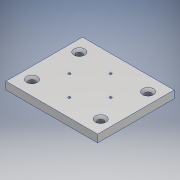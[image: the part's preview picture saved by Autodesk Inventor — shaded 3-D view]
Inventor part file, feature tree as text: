
AUTODESK INVENTOR PART (.ipt)
format: ipt  version: 2017 (Build 210142000, 142)  size: 131,072 bytes
history: native  units: mm
features: chamfer x3, sketch x3, hole x2, extrude x1
ambient origin geometry x8: Origin, YZ Plane, XZ Plane, XY Plane, X Axis, Y Axis, Z Axis, Center Point
bodies: Solid1 (feature_tree)
feature tree (9):
  extrude  "Extrusion1"  Depth=100.0mm
  hole  "Hole1"  [1 undecoded]
  chamfer  "Chamfer1"  Distance=3.0mm Angle=45.0deg
  chamfer  "Chamfer2"  Distance=3.0mm Angle=45.0deg
  hole  "Hole2"  [1 undecoded]
  chamfer  "Chamfer3"  Distance=40.0mm Angle=360.0deg
  sketch  "Sketch1"  dims[d0=120.0mm d1=100.0mm]
  sketch  "Sketch2"  dims[d3=10.0mm d4=0.0mm d5=90.0mm]
  sketch  "Sketch3"  dims[d6=62.0mm d7=8.0mm d8=6.0mm d9=4.0mm d10=2.0mm d11=90.0deg d12=8.0mm d13=20.594885mm d14=3.0mm d15=2.0mm d16=45.0deg d17=3.0mm d18=2.0mm d19=45.0deg d20=54.0mm d21=40.0mm d23=360.0deg d25=3.0mm d26=6.0mm d27=4.0mm d28=2.0mm d29=90.0deg d30=8.0mm d31=20.594885mm d32=2.0mm d33=2.0mm d34=45.0deg]
note: 2 required parameter values undecoded (feature->parameter linkage not recoverable at this tier; creation-order binding heuristic only, values carry confidence <= 0.55)
